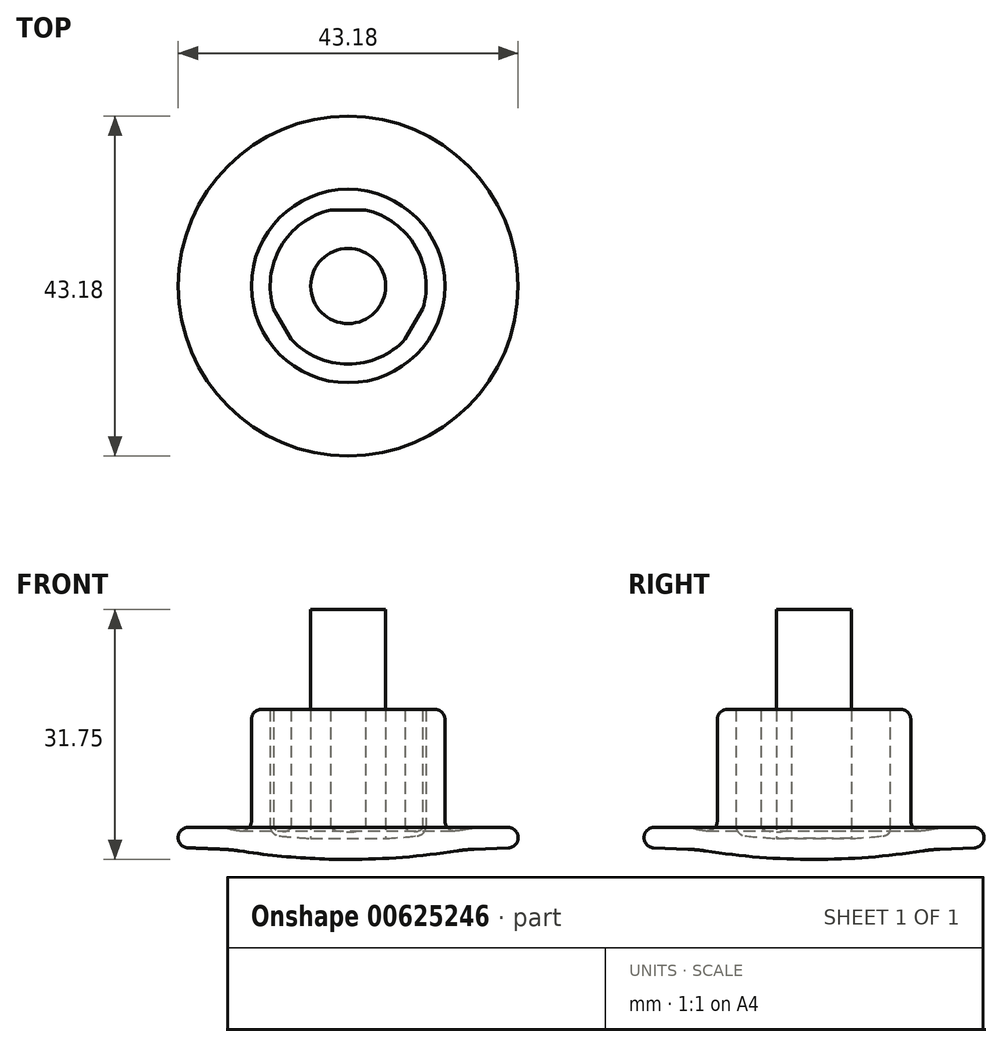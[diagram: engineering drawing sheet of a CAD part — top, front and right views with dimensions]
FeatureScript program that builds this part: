
annotation { "Feature Type Name" : "Feature", "Feature Type Description" : "" }
export const myFeature = defineFeature(function(context is Context, id is Id, definition is map)
    precondition{}
    {
        {
            var Q0;
            Q0=qCreatedBy(makeId("Front.planeOp"),FACE);
            var sketch = newSketch(context, id + "F0", { "sketchPlane" : qUnion([Q0])});
            skLineSegment(sketch, "E0", {"start": v(0, -12.45) * mm, "end": v(0, 44.47) * mm, "construction": true});
            skPoint(sketch, "E1", {"position": v(0, 88.9) * mm});
            skArc(sketch, "E2", {"start": v(-13.82, 1.08) * mm, "mid": v(-6.93, 0.27) * mm, "end": v(0, 0) * mm});
            skArc(sketch, "E3", {"start": v(-15.1, 3.87) * mm, "mid": v(-14.43, 3.75) * mm, "end": v(-13.76, 3.64) * mm});
            skLineSegment(sketch, "E4", {"start": v(-9.9, 4.25) * mm, "end": v(-9.9, 19.05) * mm});
            skLineSegment(sketch, "E5", {"start": v(-9.9, 19.05) * mm, "end": v(-11.02, 19.05) * mm});
            skLineSegment(sketch, "E6", {"start": v(-12.29, 17.78) * mm, "end": v(-12.29, 4.9) * mm});
            skLineSegment(sketch, "E7", {"start": v(0, 1.52) * mm, "end": v(-44.63, 1.52) * mm, "construction": true});
            skLineSegment(sketch, "E8", {"start": v(0, 4.06) * mm, "end": v(-44.41, 4.06) * mm, "construction": true});
            skLineSegment(sketch, "E9", {"start": v(-16.01, 1.3) * mm, "end": v(-20.37, 1.47) * mm});
            skLineSegment(sketch, "E10", {"start": v(-21.59, 2.74) * mm, "end": v(-21.59, 2.8) * mm});
            skLineSegment(sketch, "E11", {"start": v(-20.32, 4.06) * mm, "end": v(-17.3, 4.06) * mm});
            skPoint(sketch, "E12.visualSharp", {"position": v(-14.86, 1.25) * mm});
            skArc(sketch, "E12.filletArc", {"start": v(-13.82, 1.08) * mm, "mid": v(-14.91, 1.22) * mm, "end": v(-16.01, 1.3) * mm});
            skPoint(sketch, "E13.visualSharp", {"position": v(-16.15, 4.06) * mm});
            skArc(sketch, "E13.filletArc", {"start": v(-15.1, 3.87) * mm, "mid": v(-16.2, 4.02) * mm, "end": v(-17.3, 4.06) * mm});
            skArc(sketch, "E14.trimOffspring", {"start": v(-8.76, 2.99) * mm, "mid": v(-6.77, 2.8) * mm, "end": v(-4.76, 2.67) * mm});
            skPoint(sketch, "E15.visualSharp", {"position": v(-12.29, 3.42) * mm});
            skArc(sketch, "E15.filletArc", {"start": v(-13.76, 3.64) * mm, "mid": v(-12.73, 3.93) * mm, "end": v(-12.29, 4.9) * mm});
            skPoint(sketch, "E16.visualSharp", {"position": v(-9.9, 3.11) * mm});
            skArc(sketch, "E16.filletArc", {"start": v(-9.9, 4.25) * mm, "mid": v(-9.58, 3.4) * mm, "end": v(-8.76, 2.99) * mm});
            skPoint(sketch, "E17.visualSharp", {"position": v(-12.29, 19.05) * mm});
            skArc(sketch, "E17.filletArc", {"start": v(-11.02, 19.05) * mm, "mid": v(-11.92, 18.68) * mm, "end": v(-12.29, 17.78) * mm});
            skPoint(sketch, "E18.visualSharp", {"position": v(-21.59, 1.52) * mm});
            skArc(sketch, "E18.filletArc", {"start": v(-21.59, 2.74) * mm, "mid": v(-21.24, 1.86) * mm, "end": v(-20.37, 1.47) * mm});
            skPoint(sketch, "E19.visualSharp", {"position": v(-21.59, 4.06) * mm});
            skArc(sketch, "E19.filletArc", {"start": v(-20.32, 4.06) * mm, "mid": v(-21.22, 3.7) * mm, "end": v(-21.59, 2.8) * mm});
            skLineSegment(sketch, "E20", {"start": v(0, 2.54) * mm, "end": v(0, 0) * mm});
            skLineSegment(sketch, "E21", {"start": v(-4.76, 15.9) * mm, "end": v(-4.76, -6.45) * mm, "construction": true});
            skLineSegment(sketch, "E22", {"start": v(-4.76, 2.67) * mm, "end": v(-4.76, 31.75) * mm});
            skLineSegment(sketch, "E23", {"start": v(-4.76, 31.75) * mm, "end": v(0, 31.75) * mm});
            skLineSegment(sketch, "E24", {"start": v(0, 31.75) * mm, "end": v(0, 2.54) * mm});
            skSolve(sketch);
        }
        {
            var Q0;
            Q0=makeQuery(id+"F0.imprint","IMPRINT",FACE,{"disambiguationData":[TD([[makeQuery(id+"F0.imprint","IMPRINT",EDGE,{"derivedFrom":sQuery(id+"F0.wireOp",EDGE,"E2")}),1.0]])]});
            var Q1;
            Q1=sQuery(id+"F0.wireOp",EDGE,"E0");
            revolve(context, id + "F1", {"entities" : qUnion([Q0]), "axis" : qUnion([Q1]), "revolveType" : RevolveType.FULL});
        }
        {
            var Q0;
            Q0=makeQuery(id+"F1.opRevolve","SWEPT_FACE",FACE,{"disambiguationData":[OSD([sQuery(id+"F0.wireOp",EDGE,"E5")])]});
            var sketch = newSketch(context, id + "F2", { "sketchPlane" : qUnion([Q0])});
            skLineSegment(sketch, "E25.bottom", {"start": v(-2.63, 10.52) * mm, "end": v(2.58, 10.52) * mm});
            skLineSegment(sketch, "E25.top", {"start": v(-2.63, 9.65) * mm, "end": v(2.58, 9.65) * mm});
            skLineSegment(sketch, "E25.left", {"start": v(-2.63, 10.52) * mm, "end": v(-2.63, 9.65) * mm});
            skLineSegment(sketch, "E25.right", {"start": v(2.58, 10.52) * mm, "end": v(2.58, 9.65) * mm});
            skCircle(sketch, "E26", {"center": v(0, 0) * mm, "radius": 9.65 * mm, "construction": true});
            skLineSegment(sketch, "E27.1.0", {"start": v(-7.8, -7.54) * mm, "end": v(-10.4, -3.02) * mm});
            skLineSegment(sketch, "E27.1.1", {"start": v(-7.04, -7.1) * mm, "end": v(-9.65, -2.6) * mm});
            skLineSegment(sketch, "E27.1.2", {"start": v(-7.8, -7.54) * mm, "end": v(-7.04, -7.1) * mm});
            skLineSegment(sketch, "E27.1.3", {"start": v(-10.4, -3.02) * mm, "end": v(-9.65, -2.6) * mm});
            skLineSegment(sketch, "E27.2.0", {"start": v(10.42, -2.98) * mm, "end": v(7.82, -7.5) * mm});
            skLineSegment(sketch, "E27.2.1", {"start": v(9.68, -2.55) * mm, "end": v(7.07, -7.06) * mm});
            skLineSegment(sketch, "E27.2.2", {"start": v(10.42, -2.98) * mm, "end": v(9.68, -2.55) * mm});
            skLineSegment(sketch, "E27.2.3", {"start": v(7.82, -7.5) * mm, "end": v(7.07, -7.06) * mm});
            skSolve(sketch);
        }
        {
            var Q0;
            Q0 = qSketchRegion(id + "F2", true);
            extrude(context, id + "F3", {"entities" : qUnion([Q0]), "operationType" : NewBodyOperationType.ADD, "endBound" : BoundingType.UP_TO_NEXT, "oppositeDirection" : true, "depth" : 25.4 * mm, "offsetDistance" : 25.4 * mm});
        }
    });
